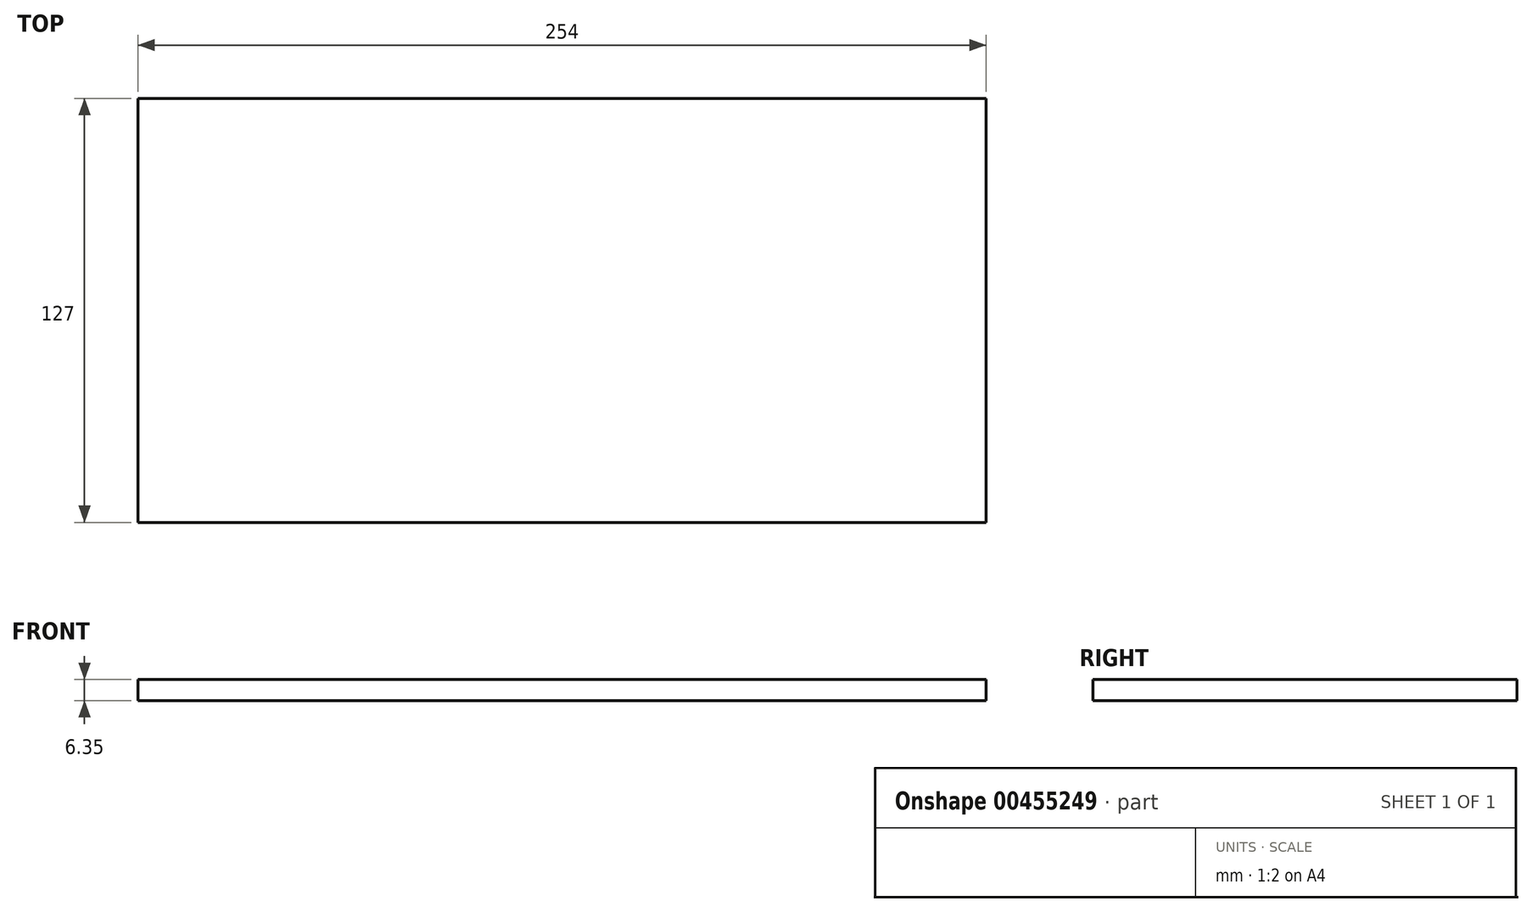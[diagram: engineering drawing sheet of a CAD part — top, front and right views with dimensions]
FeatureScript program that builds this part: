
annotation { "Feature Type Name" : "Feature", "Feature Type Description" : "" }
export const myFeature = defineFeature(function(context is Context, id is Id, definition is map)
    precondition{}
    {
        {
            var Q0;
            Q0=qCreatedBy(makeId("Top.planeOp"),FACE);
            var sketch = newSketch(context, id + "F0", { "sketchPlane" : qUnion([Q0])});
            skLineSegment(sketch, "E0.bottom", {"start": v(-138.74, 66.25) * mm, "end": v(115.26, 66.25) * mm});
            skLineSegment(sketch, "E0.top", {"start": v(-138.74, -60.75) * mm, "end": v(115.26, -60.75) * mm});
            skLineSegment(sketch, "E0.left", {"start": v(-138.74, 66.25) * mm, "end": v(-138.74, -60.75) * mm});
            skLineSegment(sketch, "E0.right", {"start": v(115.26, 66.25) * mm, "end": v(115.26, -60.75) * mm});
            skSolve(sketch);
        }
        {
            var Q0;
            Q0=makeQuery(id+"F0.imprint","IMPRINT",FACE,{"disambiguationData":[TD([[makeQuery(id+"F0.imprint","IMPRINT",EDGE,{"derivedFrom":sQuery(id+"F0.wireOp",EDGE,"E0.bottom")}),-1.0]])]});
            extrude(context, id + "F1", {"entities" : qUnion([Q0]), "depth" : 6.35 * mm});
        }
    });
